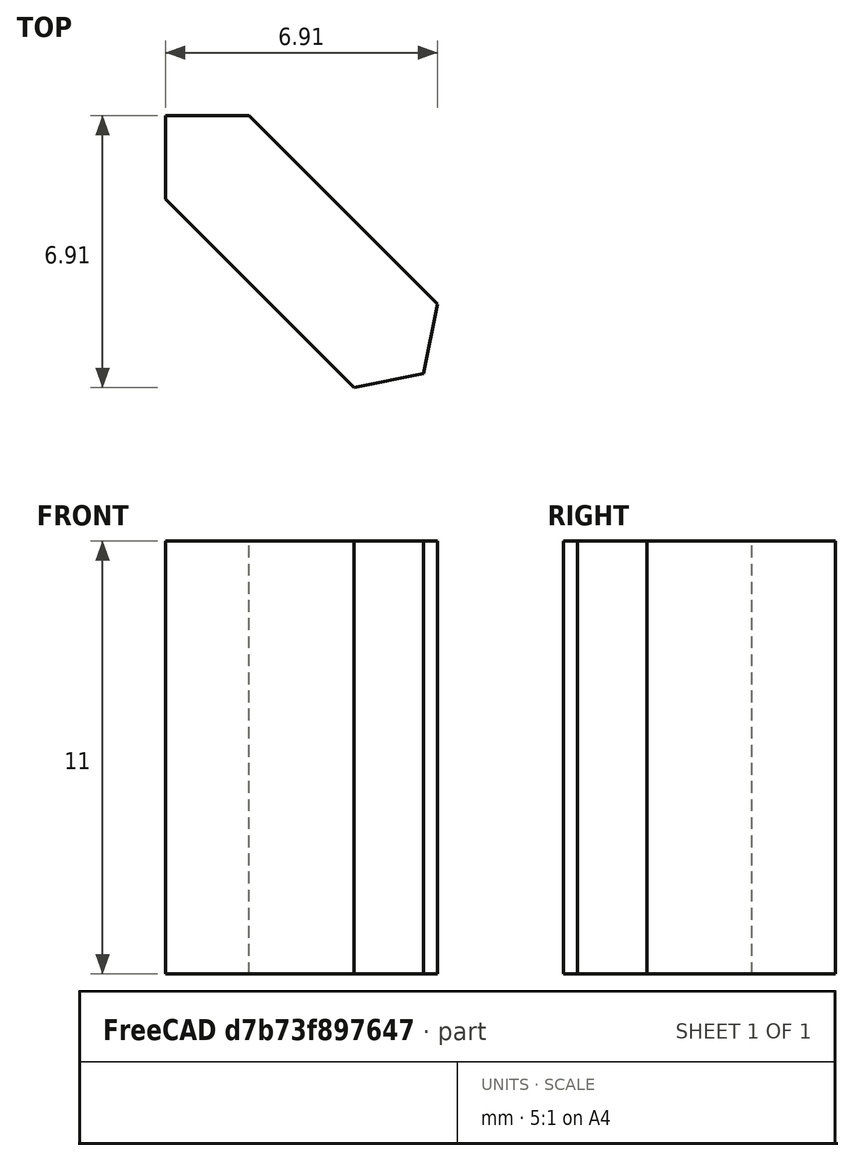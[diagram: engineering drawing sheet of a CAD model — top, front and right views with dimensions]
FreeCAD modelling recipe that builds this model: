
FCSTD DOCUMENT  (FreeCAD 0.21R33694 (Git))
Label: kumiko_inlay_short_diagonal
License: All rights reserved
LicenseURL: https://en.wikipedia.org/wiki/All_rights_reserved
objects: Sketcher::SketchObject×1, PartDesign::Pad×1, PartDesign::Body×1, App::Link×1
note: 4 computed .brp shape members not serialized (recipe doc carries the construction recipe); baked Part::Feature solids carry a one-line shape summary decoded from their .brp
EXTERNAL_REF file=../../master_kumiko_box.FCStd obj=Spreadsheet

FEATURE [Sketcher::SketchObject] Sketch099  label="short_diagonal_drawing"
  FullyConstrained = true
  MapMode = 5
  Support = -> [XY_Plane085]
  expr: Constraints[0] = 0
  expr: Constraints[10] = <<SpreadSheet>>.kumiko_thickness / sqrt(2)
  expr: Constraints[11] = (<<SpreadSheet>>.kumiko_grid_size - <<SpreadSheet>>.kumiko_thickness * (1 + sqrt(2) + 1 / sqrt(2 - sqrt(2)))) * (1 - 1 / sqrt(2))
  expr: Constraints[12] = (<<SpreadSheet>>.kumiko_grid_size - <<SpreadSheet>>.kumiko_thickness * (1 + sqrt(2) + 1 / sqrt(2 - sqrt(2)))) * (1 - 1 / sqrt(2))
  expr: Constraints[21] = 0 mm
  expr: Constraints[3] = <<SpreadSheet>>.kumiko_thickness * sqrt(2) / 2
  expr: Constraints[4] = <<SpreadSheet>>.kumiko_grid_size * (1 - 1 / sqrt(2)) - 1 / 2 * <<SpreadSheet>>.kumiko_thickness
  expr: Constraints[5] = <<SpreadSheet>>.kumiko_grid_size * (1 - 1 / sqrt(2)) - 1 / 2 * <<SpreadSheet>>.kumiko_thickness
  expr: Constraints[6] = (<<SpreadSheet>>.kumiko_grid_size - <<SpreadSheet>>.kumiko_thickness * (1 + sqrt(2) + 1 / sqrt(2 - sqrt(2)))) * (1 - 1 / sqrt(2))
  expr: Constraints[7] = (<<SpreadSheet>>.kumiko_grid_size - <<SpreadSheet>>.kumiko_thickness * (1 + sqrt(2) + 1 / sqrt(2 - sqrt(2)))) * (1 - 1 / sqrt(2))
  sketch-geometry (10):
    g0: GeomPoint X=0 Y=0 Z=0
    g1: LineSegment StartX=0 StartY=0 StartZ=0 EndX=0 EndY=-2.12132 EndZ=0
    g2: GeomPoint X=6.55456 Y=-6.55456 Z=0
    g3: GeomPoint X=4.78519 Y=-6.90651 Z=0
    g4: LineSegment StartX=0 StartY=0 StartZ=0 EndX=2.12132 EndY=0 EndZ=0
    g5: GeomPoint X=6.90651 Y=-4.78519 Z=0
    g6: LineSegment StartX=6.90651 StartY=-4.78519 StartZ=0 EndX=2.12132 EndY=0 EndZ=0
    g7: LineSegment StartX=6.90651 StartY=-4.78519 StartZ=0 EndX=6.55456 EndY=-6.55456 EndZ=0
    g8: LineSegment StartX=6.55456 StartY=-6.55456 StartZ=0 EndX=4.78519 EndY=-6.90651 EndZ=0
    g9: LineSegment StartX=4.78519 StartY=-6.90651 StartZ=0 EndX=0 EndY=-2.12132 EndZ=0
  constraints (22):
    c: DistanceX(g-1,g0) = 0
    c: Coincident(g1,g0)
    c: Vertical(g1)
    c: DistanceY(g1,g1) = 2.12132
    c: DistanceX(g1,g2) = 6.55456
    c: DistanceY(g2,g1) = 6.55456
    c: DistanceY(g3,g1) = 4.78519
    c: DistanceX(g1,g3) = 4.78519
    c: Coincident(g4,g1)
    c: Horizontal(g4)
    c: DistanceX(g4,g4) = 2.12132
    c: DistanceX(g4,g5) = 4.78519
    c: DistanceY(g5,g4) = 4.78519
    c: Coincident(g6,g5)
    c: Coincident(g6,g4)
    c: Coincident(g7,g6)
    c: Coincident(g7,g2)
    c: Coincident(g8,g7)
    c: Coincident(g8,g3)
    c: Coincident(g9,g8)
    c: Coincident(g9,g1)
    c: DistanceY(g-1,g1) = 0
FEATURE [PartDesign::Pad] Pad048  label="short_diagnoal_extrude"
  Direction = (0,0,1)
  Length = 11
  Length2 = 10
  Profile = -> Sketch099
  ReferenceAxis = -> Sketch099 [N_Axis]
  Type = 0
  expr: Length = <<SpreadSheet>>.kumiko_hight
FEATURE [PartDesign::Body] Body064  label="short_diagonal"
  Group = -> [Sketch099,Pad048]
  Origin = -> Origin085
  Tip = -> Pad048
  expr: .Placement.Base.z = 0
FEATURE [App::Link] Link  label="SpreadSheet"
  LinkedObject = -> <external ../../master_kumiko_box.FCStd>#Spreadsheet
